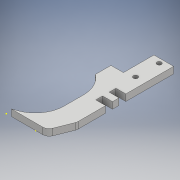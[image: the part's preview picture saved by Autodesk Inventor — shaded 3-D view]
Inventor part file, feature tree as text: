
AUTODESK INVENTOR PART (.ipt)
format: ipt  version: 2017 (Build 210142000, 142)  size: 143,872 bytes
history: native  units: mm
features: sketch x4, extrude x1, hole x1
ambient origin geometry x8: Origin, YZ Plane, XZ Plane, XY Plane, X Axis, Y Axis, Z Axis, Center Point
bodies: Solid1 (feature_tree)
feature tree (6):
  sketch  "Sketch1"  dims[d0=22.0mm d1=90.0deg]
  sketch  "Sketch2"  dims[d2=0.0mm d3=15.0mm]
  extrude  "Extrusion1"  TaperAngle=90.0deg  [1 undecoded]
  hole  "Hole1"  [1 undecoded]
  sketch  "Sketch4"  dims[d5=13.0mm d6=22.0mm d7=12.0mm d8=22.5mm d9=15.0mm d10=90.0mm d11=37.0mm d12=5.0mm d13=12.124057mm d14=5.2mm d15=5.2mm d16=5.0mm d17=7.5mm d18=5.0mm d19=0.0mm d20=18.0mm d21=7.5mm d22=7.5mm d23=3.5mm d24=3.4mm d25=6.0mm d26=4.0mm d27=2.0mm d28=90.0deg d29=8.0mm d30=20.594885mm]
  sketch  "Sketch3"  dims[d4=0.0mm]
note: 2 required parameter values undecoded (feature->parameter linkage not recoverable at this tier; creation-order binding heuristic only, values carry confidence <= 0.55)
